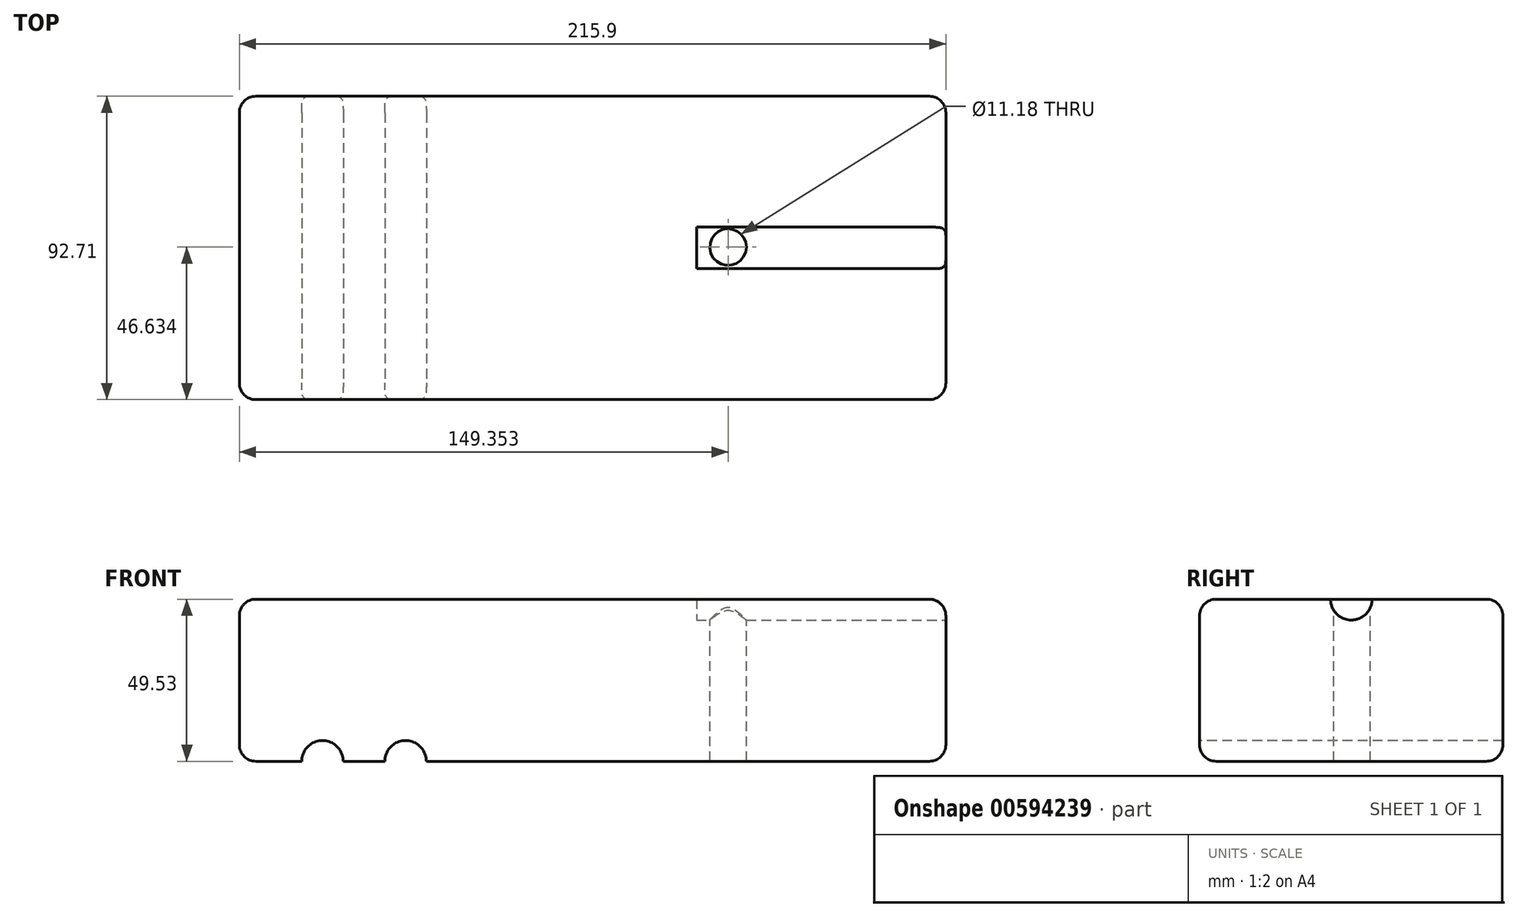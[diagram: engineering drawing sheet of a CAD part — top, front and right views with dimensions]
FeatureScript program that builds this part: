
annotation { "Feature Type Name" : "Feature", "Feature Type Description" : "" }
export const myFeature = defineFeature(function(context is Context, id is Id, definition is map)
    precondition{}
    {
        {
            var Q0;
            Q0=qCreatedBy(makeId("Top.planeOp"),FACE);
            var sketch = newSketch(context, id + "F0", { "sketchPlane" : qUnion([Q0])});
            skLineSegment(sketch, "E0.bottom", {"start": v(0, 0) * mm, "end": v(215.9, 0) * mm});
            skLineSegment(sketch, "E0.top", {"start": v(0, 92.7) * mm, "end": v(215.9, 92.7) * mm});
            skLineSegment(sketch, "E0.left", {"start": v(0, 0) * mm, "end": v(0, 92.7) * mm});
            skLineSegment(sketch, "E0.right", {"start": v(215.9, 0) * mm, "end": v(215.9, 92.7) * mm});
            skSolve(sketch);
        }
        {
            var Q0;
            Q0=makeQuery(id+"F0.imprint","IMPRINT",FACE,{"disambiguationData":[TD([[makeQuery(id+"F0.imprint","IMPRINT",EDGE,{"derivedFrom":sQuery(id+"F0.wireOp",EDGE,"E0.bottom")}),1.0]])]});
            extrude(context, id + "F1", {"entities" : qUnion([Q0]), "depth" : 49.53 * mm, "offsetDistance" : 25.4 * mm});
        }
        {
            var Q0;
            Q0=makeQuery(id+"F1.opExtrude","SWEPT_FACE",FACE,{"disambiguationData":[OSD([sQuery(id+"F0.wireOp",EDGE,"E0.right")])]});
            var sketch = newSketch(context, id + "F2", { "sketchPlane" : qUnion([Q0])});
            skArc(sketch, "E1", {"start": v(40, 49.53) * mm, "mid": v(46.35, 43.18) * mm, "end": v(52.7, 49.53) * mm});
            skLineSegment(sketch, "E2", {"start": v(40, 49.53) * mm, "end": v(52.7, 49.53) * mm});
            skSolve(sketch);
        }
        {
            var Q0;
            Q0=makeQuery(id+"F2.imprint","IMPRINT",FACE,{"disambiguationData":[TD([[makeQuery(id+"F2.imprint","IMPRINT",EDGE,{"derivedFrom":sQuery(id+"F2.wireOp",EDGE,"E1")}),1.0]])]});
            extrude(context, id + "F3", {"entities" : qUnion([Q0]), "operationType" : NewBodyOperationType.REMOVE, "oppositeDirection" : true, "depth" : 76.2 * mm, "offsetDistance" : 25.4 * mm});
        }
        {
            var Q0;
            Q0=makeQuery(id+"F1.opExtrude","SWEPT_FACE",FACE,{"disambiguationData":[OSD([sQuery(id+"F0.wireOp",EDGE,"E0.bottom")])]});
            var sketch = newSketch(context, id + "F4", { "sketchPlane" : qUnion([Q0])});
            skArc(sketch, "E3", {"start": v(31.75, 0) * mm, "mid": v(25.4, 6.35) * mm, "end": v(19.05, 0) * mm});
            skLineSegment(sketch, "E4", {"start": v(19.05, 0) * mm, "end": v(31.75, 0) * mm});
            skSolve(sketch);
        }
        {
            var Q0;
            Q0=makeQuery(id+"F4.imprint","IMPRINT",FACE,{"disambiguationData":[TD([[makeQuery(id+"F4.imprint","IMPRINT",EDGE,{"derivedFrom":sQuery(id+"F4.wireOp",EDGE,"E3")}),1.0]])]});
            extrude(context, id + "F5", {"entities" : qUnion([Q0]), "operationType" : NewBodyOperationType.REMOVE, "endBound" : BoundingType.UP_TO_NEXT, "oppositeDirection" : true, "depth" : 25.4 * mm, "offsetDistance" : 25.4 * mm});
        }
        {
            var Q0;
            Q0=makeQuery(id+"F1.opExtrude","CAP_EDGE",EDGE,{"disambiguationData":[OSD([sQuery(id+"F0.wireOp",EDGE,"E0.bottom")])],"isStart":false});
            var Q1;
            {var subQ0=sQuery(id+"F0.wireOp",EDGE,"E0.bottom");var subQ1=sQuery(id+"F0.wireOp",EDGE,"E0.right");Q1=makeQuery(id+"F3.boolean.opBoolean","SPLIT",EDGE,{"disambiguationData":[TD([makeQuery(id+"F1.opExtrude","SWEPT_FACE",FACE,{"disambiguationData":[OSD([subQ0])]})])],"derivedFrom":makeQuery(id+"F1.opExtrude","CAP_EDGE",EDGE,{"disambiguationData":[OSD([subQ1])],"isStart":false})});}
            var Q2;
            Q2=makeQuery(id+"F1.opExtrude","CAP_EDGE",EDGE,{"disambiguationData":[OSD([sQuery(id+"F0.wireOp",EDGE,"E0.top")])],"isStart":false});
            var Q3;
            {var subQ0=sQuery(id+"F0.wireOp",EDGE,"E0.right");var subQ1=sQuery(id+"F0.wireOp",EDGE,"E0.top");Q3=makeQuery(id+"F3.boolean.opBoolean","SPLIT",EDGE,{"disambiguationData":[TD([makeQuery(id+"F1.opExtrude","SWEPT_FACE",FACE,{"disambiguationData":[OSD([subQ1])]})])],"derivedFrom":makeQuery(id+"F1.opExtrude","CAP_EDGE",EDGE,{"disambiguationData":[OSD([subQ0])],"isStart":false})});}
            var Q4;
            Q4=makeQuery(id+"F1.opExtrude","SWEPT_EDGE",EDGE,{"disambiguationData":[OSD([sQuery(id+"F0.wireOp",EDGE,"E0.top"),sQuery(id+"F0.wireOp",EDGE,"E0.left")])]});
            var Q5;
            Q5=makeQuery(id+"F1.opExtrude","CAP_EDGE",EDGE,{"disambiguationData":[OSD([sQuery(id+"F0.wireOp",EDGE,"E0.left")])],"isStart":false});
            var Q6;
            Q6=makeQuery(id+"F1.opExtrude","SWEPT_EDGE",EDGE,{"disambiguationData":[OSD([sQuery(id+"F0.wireOp",EDGE,"E0.bottom"),sQuery(id+"F0.wireOp",EDGE,"E0.left")])]});
            var Q7;
            Q7=makeQuery(id+"F1.opExtrude","CAP_EDGE",EDGE,{"disambiguationData":[OSD([sQuery(id+"F0.wireOp",EDGE,"E0.left")])],"isStart":true});
            var Q8;
            {var subQ0=sQuery(id+"F0.wireOp",EDGE,"E0.bottom");var subQ1=sQuery(id+"F0.wireOp",EDGE,"E0.right");Q8=makeQuery(id+"F5.boolean.opBoolean","SPLIT",EDGE,{"disambiguationData":[TD([makeQuery(id+"F1.opExtrude","SWEPT_FACE",FACE,{"disambiguationData":[OSD([subQ1])]})])],"derivedFrom":makeQuery(id+"F1.opExtrude","CAP_EDGE",EDGE,{"disambiguationData":[OSD([subQ0])],"isStart":true})});}
            var Q9;
            {var subQ0=sQuery(id+"F0.wireOp",EDGE,"E0.right");var subQ1=sQuery(id+"F0.wireOp",EDGE,"E0.top");Q9=makeQuery(id+"F5.boolean.opBoolean","SPLIT",EDGE,{"disambiguationData":[TD([makeQuery(id+"F1.opExtrude","SWEPT_FACE",FACE,{"disambiguationData":[OSD([subQ0])]})])],"derivedFrom":makeQuery(id+"F1.opExtrude","CAP_EDGE",EDGE,{"disambiguationData":[OSD([subQ1])],"isStart":true})});}
            var Q10;
            Q10=makeQuery(id+"F1.opExtrude","CAP_EDGE",EDGE,{"disambiguationData":[OSD([sQuery(id+"F0.wireOp",EDGE,"E0.right")])],"isStart":true});
            var Q11;
            Q11=makeQuery(id+"F1.opExtrude","SWEPT_EDGE",EDGE,{"disambiguationData":[OSD([sQuery(id+"F0.wireOp",EDGE,"E0.top"),sQuery(id+"F0.wireOp",EDGE,"E0.right")])]});
            var Q12;
            Q12=makeQuery(id+"F1.opExtrude","SWEPT_EDGE",EDGE,{"disambiguationData":[OSD([sQuery(id+"F0.wireOp",EDGE,"E0.bottom"),sQuery(id+"F0.wireOp",EDGE,"E0.right")])]});
            fillet(context, id + "F6", {"entities" : qUnion([Q0, Q1, Q2, Q3, Q4, Q5, Q6, Q7, Q8, Q9, Q10, Q11, Q12]), "radius" : 5.08 * mm, "tangentPropagation" : true, "allowEdgeOverflow" : false});
        }
        {
            var Q0;
            Q0=qCreatedBy(makeId("Front.planeOp"),FACE);
            var sketch = newSketch(context, id + "F7", { "sketchPlane" : qUnion([Q0])});
            skCircle(sketch, "E5", {"center": v(50.8, 0) * mm, "radius": 6.35 * mm});
            skSolve(sketch);
        }
        {
            var Q0;
            Q0=makeQuery(id+"F7.imprint","IMPRINT",FACE,{"disambiguationData":[TD([[makeQuery(id+"F7.imprint","IMPRINT",EDGE,{"derivedFrom":sQuery(id+"F7.wireOp",EDGE,"E5")}),1.0]])]});
            extrude(context, id + "F8", {"entities" : qUnion([Q0]), "operationType" : NewBodyOperationType.REMOVE, "endBound" : BoundingType.THROUGH_ALL, "oppositeDirection" : true, "depth" : 25.4 * mm, "offsetDistance" : 25.4 * mm});
        }
        {
            var Q0;
            {var subQ0=sQuery(id+"F0.wireOp",EDGE,"E0.bottom");var subQ1=sQuery(id+"F0.wireOp",EDGE,"E0.left");Q0=makeQuery(id+"F5.boolean.opBoolean","SPLIT",EDGE,{"disambiguationData":[TD([makeQuery(id+"F1.opExtrude","SWEPT_FACE",FACE,{"disambiguationData":[OSD([subQ1])]})])],"derivedFrom":makeQuery(id+"F1.opExtrude","CAP_EDGE",EDGE,{"disambiguationData":[OSD([subQ0])],"isStart":true})});}
            var Q1;
            {var subQ0=sQuery(id+"F0.wireOp",EDGE,"E0.left");var subQ1=sQuery(id+"F0.wireOp",EDGE,"E0.top");Q1=makeQuery(id+"F5.boolean.opBoolean","SPLIT",EDGE,{"disambiguationData":[TD([makeQuery(id+"F1.opExtrude","SWEPT_FACE",FACE,{"disambiguationData":[OSD([subQ0])]})])],"derivedFrom":makeQuery(id+"F1.opExtrude","CAP_EDGE",EDGE,{"disambiguationData":[OSD([subQ1])],"isStart":true})});}
            fillet(context, id + "F9", {"entities" : qUnion([Q0, Q1]), "radius" : 5.08 * mm, "tangentPropagation" : true, "allowEdgeOverflow" : false});
        }
        {
            var Q0;
            Q0=makeQuery(id+"F1.opExtrude","CAP_FACE",FACE,{"disambiguationData":[OSD([sQuery(id+"F0.wireOp",EDGE,"E0.bottom"),sQuery(id+"F0.wireOp",EDGE,"E0.top"),sQuery(id+"F0.wireOp",EDGE,"E0.left"),sQuery(id+"F0.wireOp",EDGE,"E0.right")])],"isStart":false});
            var sketch = newSketch(context, id + "F10", { "sketchPlane" : qUnion([Q0])});
            skCircle(sketch, "E6", {"center": v(149.35, 46.63) * mm, "radius": 5.59 * mm});
            skSolve(sketch);
        }
        {
            var Q0;
            Q0=makeQuery(id+"F10.imprint","IMPRINT",FACE,{"disambiguationData":[TD([[makeQuery(id+"F10.imprint","IMPRINT",EDGE,{"derivedFrom":sQuery(id+"F10.wireOp",EDGE,"E6")}),1.0]])]});
            extrude(context, id + "F11", {"entities" : qUnion([Q0]), "operationType" : NewBodyOperationType.REMOVE, "endBound" : BoundingType.THROUGH_ALL, "oppositeDirection" : true, "depth" : 25.4 * mm, "offsetDistance" : 25.4 * mm});
        }
    });
